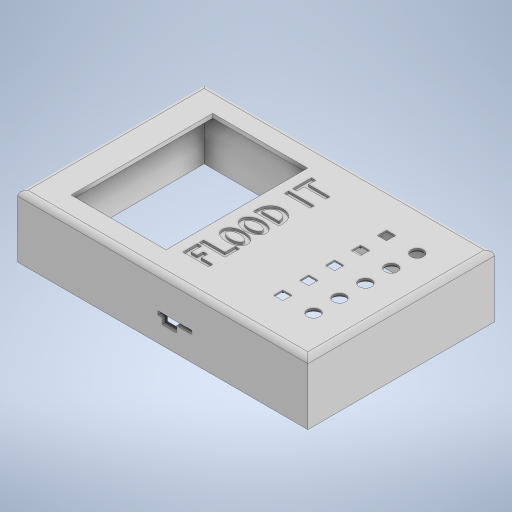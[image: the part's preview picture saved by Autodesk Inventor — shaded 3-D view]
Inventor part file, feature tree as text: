
AUTODESK INVENTOR PART (.ipt)
format: ipt  version: 2023 (Build 270158000, 158)  size: 669,696 bytes
history: native  units: in
note: dims shown in document units (in); Inventor stores cm internally (conversion verified against a paired STEP export)
features: extrude x15, sketch x13, fillet x2
ambient origin geometry x8: Origin, YZ Plane, XZ Plane, XY Plane, X Axis, Y Axis, Z Axis, Center Point
bodies: Solid1 (feature_tree)
feature tree (30):
  extrude  "Extrusion1"  Depth=4.5in
  extrude  "Extrusion2"  Depth=0.2in
  fillet  "Fillet1"  Radius=1.4in
  extrude  "Extrusion3"  Depth=0.25in
  extrude  "Extrusion4"  Depth=2.2875in
  extrude  "Extrusion5"  Depth=0.5437in
  sketch  "Sketch6"  dims[d13=0.75in d14=1.4in d15=0.0in]
  extrude  "Extrusion6"  Depth=1.4in TaperAngle=0.0deg
  extrude  "Extrusion9"  Depth=0.1in
  extrude  "Extrusion10"  Depth=0.275in
  extrude  "Extrusion11"  Depth=0.25in
  extrude  "Extrusion12"  Depth=0.15in
  extrude  "Extrusion13"  Depth=0.7in
  extrude  "Extrusion14"  Depth=0.1in
  extrude  "Extrusion15"  Depth=2.8in
  extrude  "Extrusion16"  Depth=0.25in
  fillet  "Fillet2"  Radius=1.1in
  extrude  "Extrusion17"  Depth=2.8in
  sketch  "Sketch1"  dims[d0=7.0in d1=4.5in]
  sketch  "Sketch2"  dims[d2=1.5in d3=0.0in d4=0.2in d5=1.4in d6=0.0in]
  sketch  "Sketch3"  dims[d7=0.125in d8=0.25in]
  sketch  "Sketch4"  dims[d9=0.25in d10=2.2875in]
  sketch  "Sketch5"  dims[d11=3.4125in d12=0.5437in]
  sketch  "Sketch8"  dims[d16=0.1in d17=0.14in]
  sketch  "Sketch9"  dims[d18=0.1in d19=0.275in]
  sketch  "Sketch10"  dims[d20=0.35in d21=0.25in]
  sketch  "Sketch11"  dims[d22=0.15in d23=0.15in]
  sketch  "Sketch12"  dims[d24=0.25in d25=0.7in]
  sketch  "Sketch13"  dims[d26=0.1in d27=0.1in]
  sketch  "Sketch14"  dims[d28=0.25in d29=0.615in d30=0.25in d31=1.1in d32=0.21in d33=0.3075in d34=0.5575in d35=1.65in d36=0.3075in d37=0.21in d38=0.5575in d39=2.1in d40=0.1in d41=0.1in d42=0.3in d43=0.1in d44=0.25in d45=0.615in d46=2.4in d47=0.11in d48=2.51in d49=0.5575in d50=0.1in d51=0.615in d52=0.175in d53=0.175in d54=0.1in d55=0.1in d56=0.25in d57=3.15in d58=0.1in d59=0.515in d60=0.05in d61=0.0in d62=0.1562in d63=0.1562in d64=0.2188in d65=0.2188in d66=0.2188in d67=0.2188in d68=0.2188in d69=0.2188in d70=0.625in d71=0.625in d72=0.625in d73=0.625in d74=0.8906in d76=2.25in d77=0.3in d78=0.3in d79=0.3in d80=0.3in d81=0.3in d82=0.625in d83=0.625in d84=0.625in d85=0.625in d86=1.0in d87=3.1in d88=3.1in d89=3.1in d90=3.1in d91=3.1in d92=1.0in d93=0.0in d97=0.4in d98=0.4in d99=0.4in d100=0.4in d101=0.4in d102=0.05in d103=0.0in d119=0.075in d120=0.075in d121=0.075in d122=0.075in d123=0.075in d124=0.0688in d125=0.0in d126=0.25in d127=0.275in d128=0.25in d129=0.25in d130=0.25in d131=2.1in d132=0.125in d133=0.0625in d134=0.05in d135=0.0in d136=0.6in d137=3.35in d139=0.3in d140=0.3155in d141=0.3157in d142=0.0375in d143=0.0in d144=2.0in d145=0.8125in d146=0.0825in d147=0.35in d148=0.15in d149=0.1in d150=0.7in d151=0.2in d152=0.0in d153=0.075in d154=0.125in d155=0.0in d156=0.3in d157=2.5in d158=0.5in d159=0.25in d160=0.0in d161=0.5in d162=0.081in d163=0.0in d164=0.45in d165=0.6in d166=0.2in d167=0.2in d168=0.2in d169=0.075in d170=0.075in d171=0.075in d172=0.075in d173=0.2in d174=0.2in d175=0.2in d176=0.2in d177=0.075in d178=0.0in d179=0.125in d180=0.0375in d181=0.0375in d182=2.0in d183=0.5in d184=0.0in d185=0.0in d187=2.8in]
